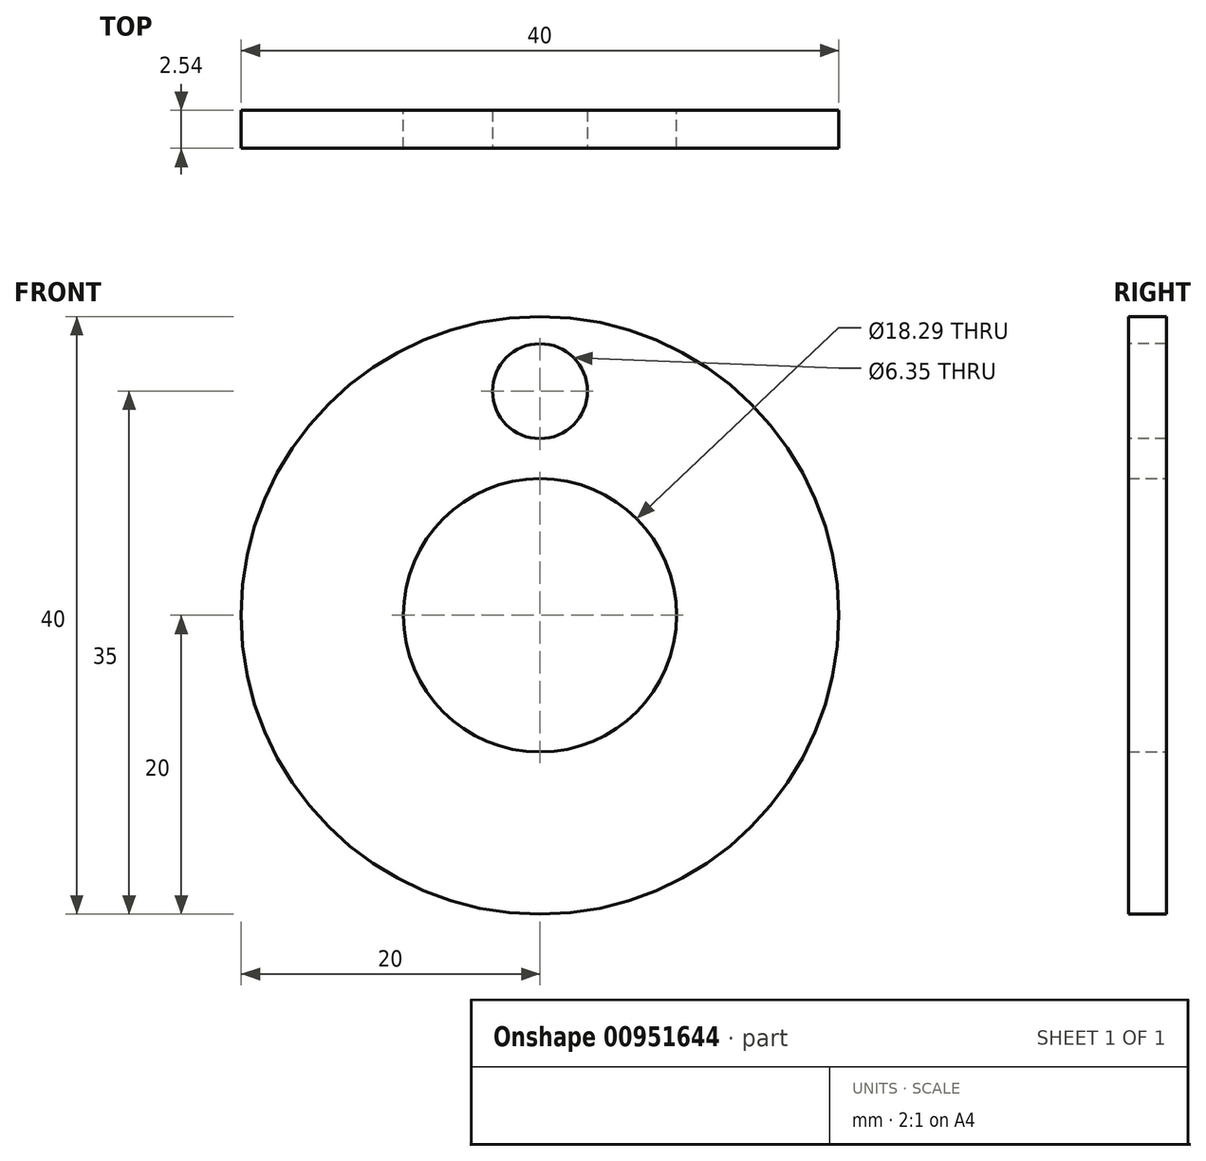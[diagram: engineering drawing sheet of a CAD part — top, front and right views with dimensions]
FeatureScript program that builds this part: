
annotation { "Feature Type Name" : "Feature", "Feature Type Description" : "" }
export const myFeature = defineFeature(function(context is Context, id is Id, definition is map)
    precondition{}
    {
        {
            var Q0;
            Q0=qCreatedBy(makeId("Front.planeOp"),FACE);
            var sketch = newSketch(context, id + "F0", { "sketchPlane" : qUnion([Q0])});
            skCircle(sketch, "E0", {"center": v(0, 0) * mm, "radius": 20 * mm});
            skSolve(sketch);
        }
        {
            var Q0;
            Q0=qSketchRegion(id+"F0",true);
            extrude(context, id + "F1", {"entities" : qUnion([Q0]), "depth" : 2.54 * mm, "offsetDistance" : 25 * mm});
        }
        {
            var Q0;
            Q0=makeQuery(id+"F1.opExtrude","CAP_FACE",FACE,{"disambiguationData":[OSD([sQuery(id+"F0.wireOp",EDGE,"E0")])],"isStart":true});
            var sketch = newSketch(context, id + "F2", { "sketchPlane" : qUnion([Q0])});
            skCircle(sketch, "E1", {"center": v(0, 0) * mm, "radius": 9.14 * mm});
            skSolve(sketch);
        }
        {
            var Q0;
            Q0=qSketchRegion(id+"F2",true);
            extrude(context, id + "F3", {"entities" : qUnion([Q0]), "operationType" : NewBodyOperationType.REMOVE, "oppositeDirection" : true, "depth" : 8.5 * mm, "offsetDistance" : 25 * mm});
        }
        {
            var Q0;
            Q0=makeQuery(id+"F1.opExtrude","CAP_FACE",FACE,{"disambiguationData":[OSD([sQuery(id+"F0.wireOp",EDGE,"E0")])],"isStart":false});
            var sketch = newSketch(context, id + "F4", { "sketchPlane" : qUnion([Q0])});
            skCircle(sketch, "E2", {"center": v(0, 15) * mm, "radius": 3.18 * mm});
            skSolve(sketch);
        }
        {
            var Q0;
            Q0=qSketchRegion(id+"F4",true);
            extrude(context, id + "F5", {"entities" : qUnion([Q0]), "operationType" : NewBodyOperationType.REMOVE, "endBound" : BoundingType.THROUGH_ALL, "oppositeDirection" : true, "depth" : 25 * mm, "offsetDistance" : 25 * mm});
        }
    });
